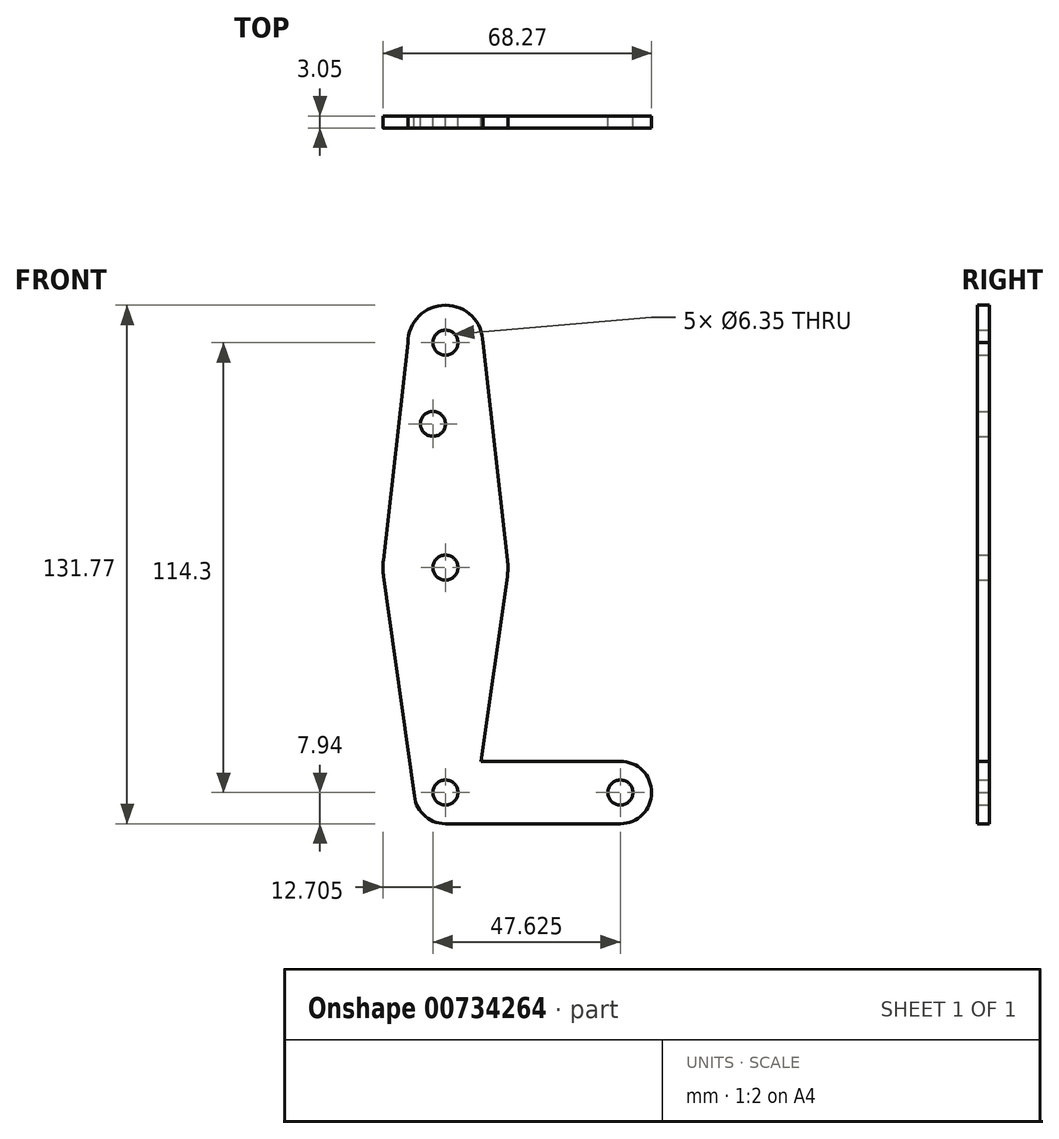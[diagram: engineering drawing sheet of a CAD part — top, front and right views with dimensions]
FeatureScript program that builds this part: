
annotation { "Feature Type Name" : "Feature", "Feature Type Description" : "" }
export const myFeature = defineFeature(function(context is Context, id is Id, definition is map)
    precondition{}
    {
        {
            var Q0;
            Q0=qCreatedBy(makeId("Front.planeOp"),FACE);
            var sketch = newSketch(context, id + "F0", { "sketchPlane" : qUnion([Q0])});
            skLineSegment(sketch, "E0", {"start": v(0, 0) * mm, "end": v(0, 114.3) * mm, "construction": true});
            skLineSegment(sketch, "E1", {"start": v(0, 0) * mm, "end": v(44.45, 0) * mm, "construction": true});
            skCircle(sketch, "E2", {"center": v(0, 114.3) * mm, "radius": 9.53 * mm});
            skCircle(sketch, "E3", {"center": v(0, 57.15) * mm, "radius": 15.88 * mm});
            skCircle(sketch, "E4", {"center": v(0, 0) * mm, "radius": 7.94 * mm});
            skCircle(sketch, "E5", {"center": v(44.45, 0) * mm, "radius": 7.94 * mm});
            skLineSegment(sketch, "E6", {"start": v(7.94, 0) * mm, "end": v(15.72, 54.92) * mm});
            skLineSegment(sketch, "E7", {"start": v(-7.94, 0) * mm, "end": v(-15.72, 54.92) * mm});
            skLineSegment(sketch, "E8", {"start": v(9.52, 114.3) * mm, "end": v(15.77, 58.93) * mm});
            skLineSegment(sketch, "E9", {"start": v(-9.52, 114.3) * mm, "end": v(-15.77, 58.93) * mm});
            skLineSegment(sketch, "E10", {"start": v(44.45, 7.94) * mm, "end": v(0, 7.94) * mm});
            skLineSegment(sketch, "E11", {"start": v(44.45, -7.94) * mm, "end": v(0, -7.94) * mm});
            skCircle(sketch, "E12", {"center": v(0, 114.3) * mm, "radius": 3.18 * mm});
            skCircle(sketch, "E13", {"center": v(0, 57.15) * mm, "radius": 3.18 * mm});
            skCircle(sketch, "E14", {"center": v(0, 0) * mm, "radius": 3.18 * mm});
            skCircle(sketch, "E15", {"center": v(44.45, 0) * mm, "radius": 3.18 * mm});
            skCircle(sketch, "E16", {"center": v(-3.18, 93.68) * mm, "radius": 3.18 * mm});
            skSolve(sketch);
        }
        {
            var Q0;
            Q0 = qSketchRegion(id + "F0", true);
            extrude(context, id + "F1", {"entities" : qUnion([Q0]), "depth" : 3.05 * mm, "offsetDistance" : 25.4 * mm});
        }
    });
